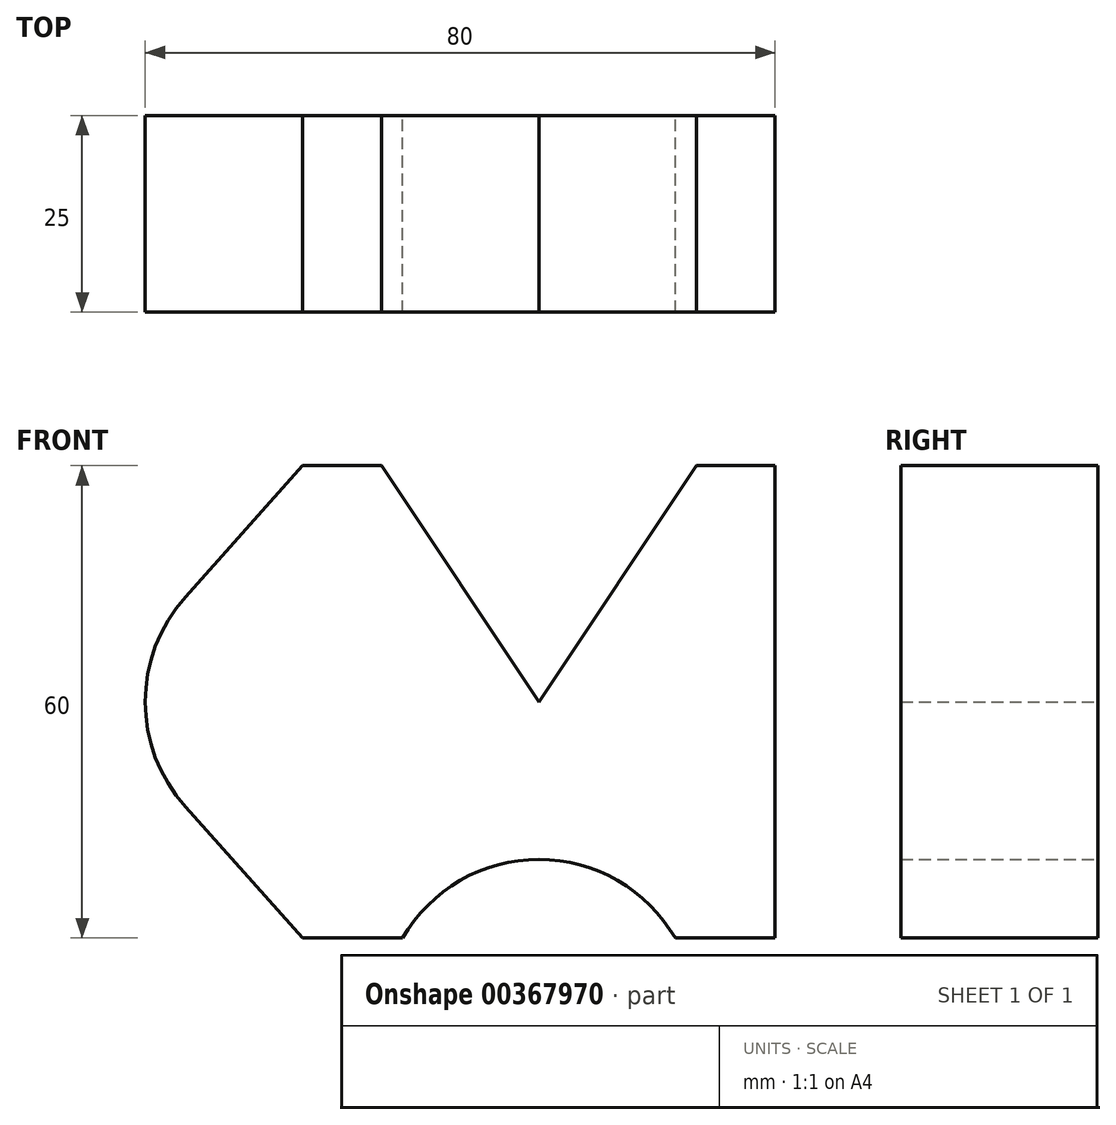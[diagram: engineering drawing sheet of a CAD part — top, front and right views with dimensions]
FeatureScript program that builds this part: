
annotation { "Feature Type Name" : "Feature", "Feature Type Description" : "" }
export const myFeature = defineFeature(function(context is Context, id is Id, definition is map)
    precondition{}
    {
        {
            var Q0;
            Q0=qCreatedBy(makeId("Front.planeOp"),FACE);
            var sketch = newSketch(context, id + "F0", { "sketchPlane" : qUnion([Q0])});
            skLineSegment(sketch, "E0", {"start": v(0, 0) * mm, "end": v(20, 30) * mm});
            skLineSegment(sketch, "E1", {"start": v(20, 30) * mm, "end": v(30, 30) * mm});
            skLineSegment(sketch, "E2", {"start": v(30, 30) * mm, "end": v(30, -30) * mm});
            skLineSegment(sketch, "E3", {"start": v(30, -30) * mm, "end": v(17.32, -30) * mm});
            skArc(sketch, "E4", {"start": v(17.32, -30) * mm, "mid": v(0, -20) * mm, "end": v(-17.32, -30) * mm});
            skLineSegment(sketch, "E5", {"start": v(-17.32, -30) * mm, "end": v(-30, -30) * mm});
            skLineSegment(sketch, "E6", {"start": v(-30, -30) * mm, "end": v(-44.9, -13.33) * mm});
            skArc(sketch, "E7", {"start": v(-44.9, 13.33) * mm, "mid": v(-50, 0) * mm, "end": v(-44.9, -13.33) * mm});
            skLineSegment(sketch, "E8", {"start": v(-44.9, 13.33) * mm, "end": v(-30, 30) * mm});
            skLineSegment(sketch, "E9", {"start": v(-30, 30) * mm, "end": v(-20, 30) * mm});
            skLineSegment(sketch, "E10", {"start": v(-20, 30) * mm, "end": v(0, 0) * mm});
            skLineSegment(sketch, "E11", {"start": v(-30, 30) * mm, "end": v(-30, -30) * mm, "construction": true});
            skSolve(sketch);
        }
        {
            var Q0;
            Q0=makeQuery(id+"F0.imprint","IMPRINT",FACE,{"disambiguationData":[TD([[makeQuery(id+"F0.imprint","IMPRINT",EDGE,{"derivedFrom":sQuery(id+"F0.wireOp",EDGE,"E0")}),-1.0]])]});
            extrude(context, id + "F1", {"entities" : qUnion([Q0]), "depth" : 25 * mm});
        }
    });
